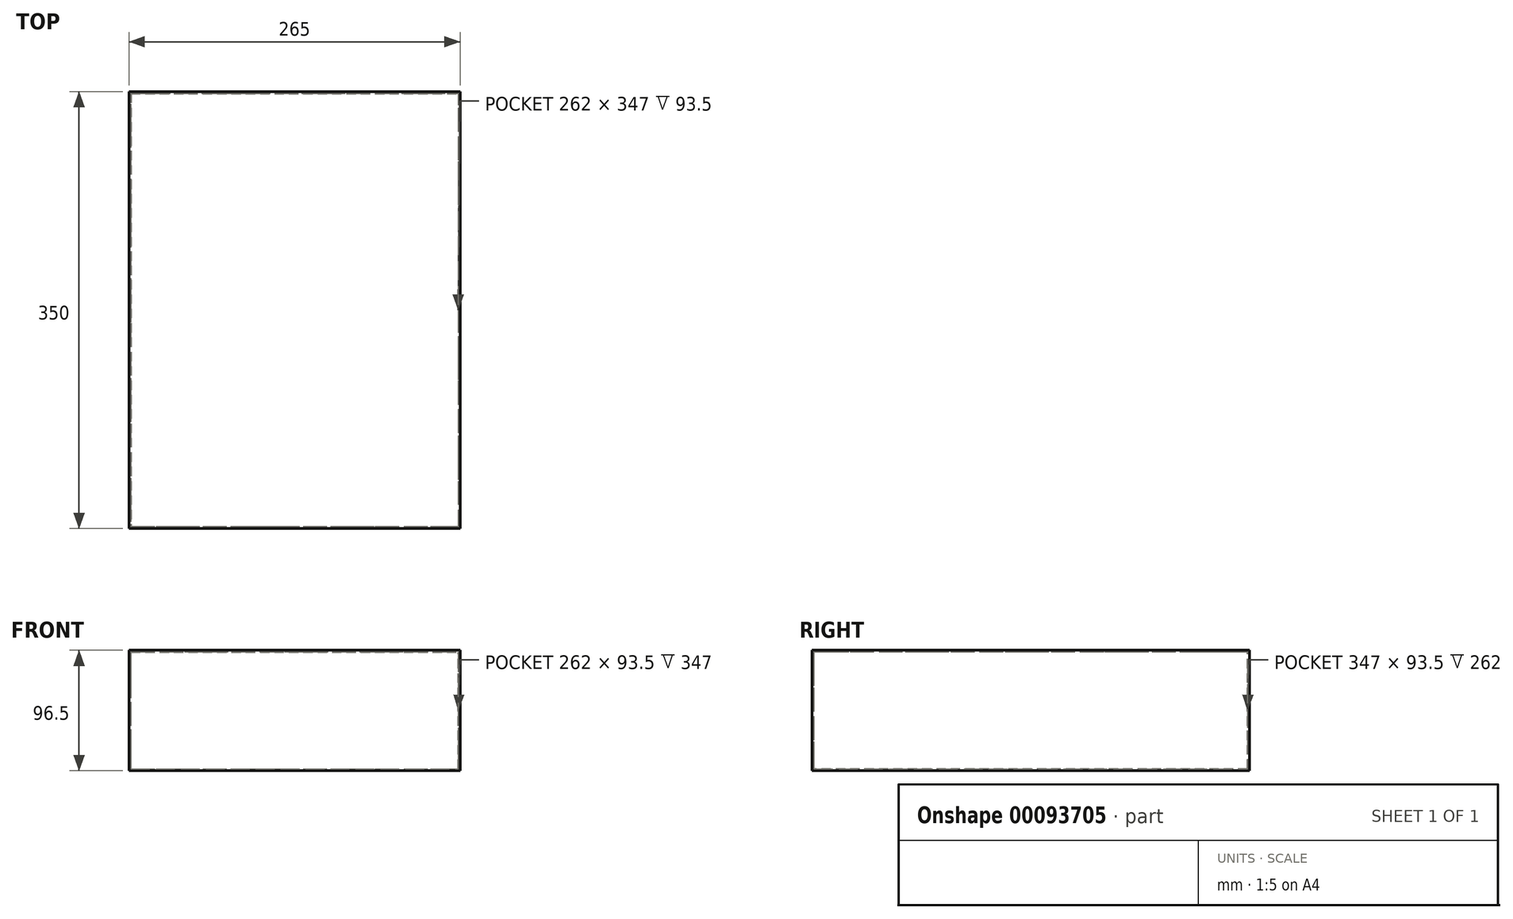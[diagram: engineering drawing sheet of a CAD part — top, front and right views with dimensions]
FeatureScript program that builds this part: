
annotation { "Feature Type Name" : "Feature", "Feature Type Description" : "" }
export const myFeature = defineFeature(function(context is Context, id is Id, definition is map)
    precondition{}
    {
        {
            var Q0;
            Q0=qCreatedBy(makeId("Front.planeOp"),FACE);
            var sketch = newSketch(context, id + "F0", { "sketchPlane" : qUnion([Q0])});
            skLineSegment(sketch, "E0.bottom", {"start": v(0, 0) * mm, "end": v(265, 0) * mm});
            skLineSegment(sketch, "E0.top", {"start": v(0, 95) * mm, "end": v(265, 95) * mm});
            skLineSegment(sketch, "E0.left", {"start": v(0, 0) * mm, "end": v(0, 95) * mm});
            skLineSegment(sketch, "E0.right", {"start": v(265, 0) * mm, "end": v(265, 95) * mm});
            skSolve(sketch);
        }
        {
            var Q0;
            Q0=makeQuery(id+"F0.imprint","IMPRINT",FACE,{"disambiguationData":[TD([[makeQuery(id+"F0.imprint","IMPRINT",EDGE,{"derivedFrom":sQuery(id+"F0.wireOp",EDGE,"E0.bottom")}),1.0]])]});
            extrude(context, id + "F1", {"entities" : qUnion([Q0]), "oppositeDirection" : true, "depth" : 350 * mm, "offsetDistance" : 25 * mm});
        }
        {
            var Q0;
            Q0=makeQuery(id+"F1.opExtrude","SWEPT_FACE",FACE,{"disambiguationData":[OSD([sQuery(id+"F0.wireOp",EDGE,"E0.top")])]});
            shell(context, id + "F2", {"entities" : qUnion([Q0]), "thickness" : 1.5 * mm});
        }
        {
            var Q0;
            Q0=makeQuery(id+"F1.opExtrude","SWEPT_FACE",FACE,{"disambiguationData":[OSD([sQuery(id+"F0.wireOp",EDGE,"E0.top")])]});
            var sketch = newSketch(context, id + "F3", { "sketchPlane" : qUnion([Q0])});
            skLineSegment(sketch, "E1.bottom", {"start": v(0, 0) * mm, "end": v(265, 0) * mm});
            skLineSegment(sketch, "E1.top", {"start": v(0, 350) * mm, "end": v(265, 350) * mm});
            skLineSegment(sketch, "E1.left", {"start": v(0, 0) * mm, "end": v(0, 350) * mm});
            skLineSegment(sketch, "E1.right", {"start": v(265, 0) * mm, "end": v(265, 350) * mm});
            skSolve(sketch);
        }
        {
            var Q0;
            Q0 = qSketchRegion(id + "F3", true);
            extrude(context, id + "F4", {"entities" : qUnion([Q0]), "operationType" : NewBodyOperationType.ADD, "depth" : 1.5 * mm, "offsetDistance" : 25 * mm});
        }
    });
